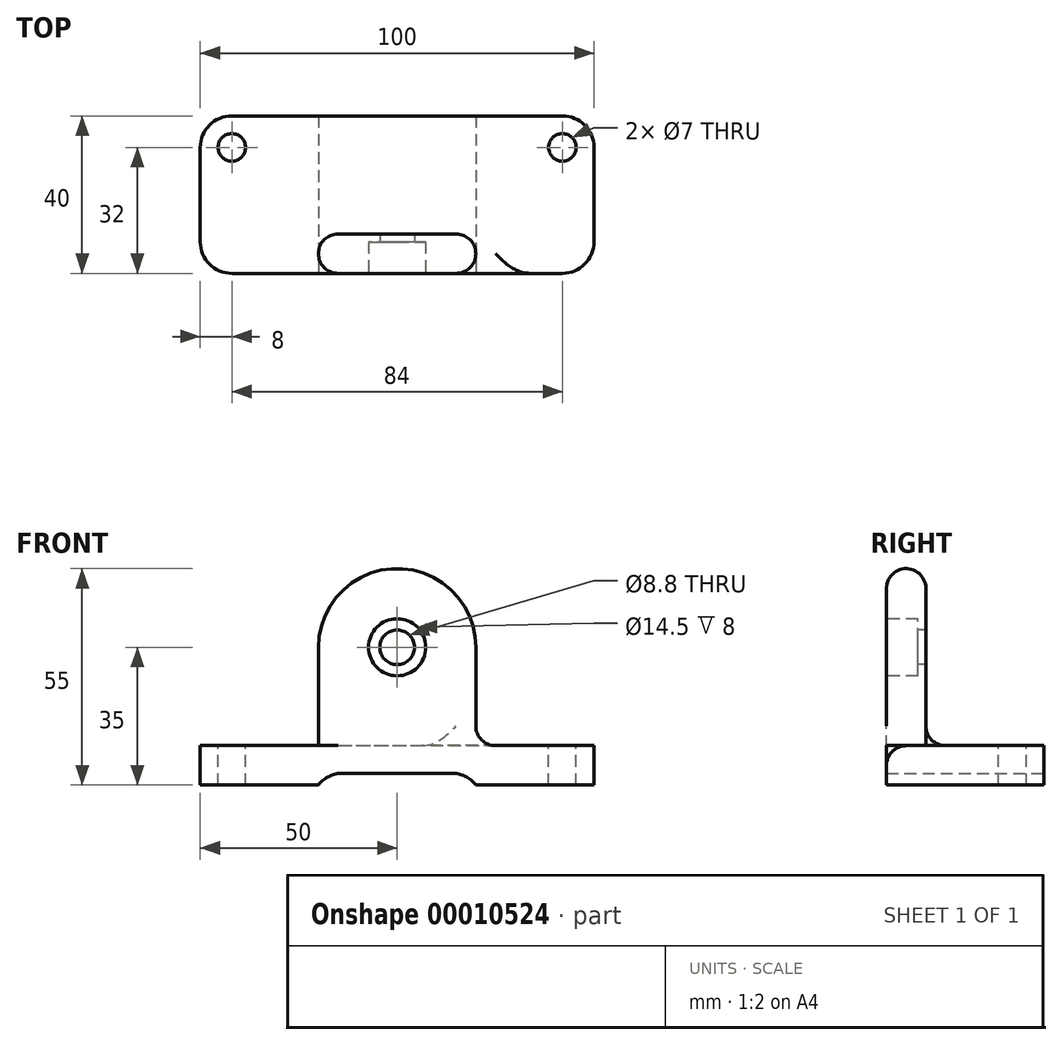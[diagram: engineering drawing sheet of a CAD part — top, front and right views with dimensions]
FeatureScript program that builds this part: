
annotation { "Feature Type Name" : "Feature", "Feature Type Description" : "" }
export const myFeature = defineFeature(function(context is Context, id is Id, definition is map)
    precondition{}
    {
        {
            var Q0;
            Q0=qCreatedBy(makeId("Top.planeOp"),FACE);
            var sketch = newSketch(context, id + "F0", { "sketchPlane" : qUnion([Q0])});
            skLineSegment(sketch, "E0.bottom", {"start": v(0, 0) * mm, "end": v(100, 0) * mm});
            skLineSegment(sketch, "E0.top", {"start": v(0, 40) * mm, "end": v(100, 40) * mm});
            skLineSegment(sketch, "E0.left", {"start": v(0, 0) * mm, "end": v(0, 40) * mm});
            skLineSegment(sketch, "E0.right", {"start": v(100, 0) * mm, "end": v(100, 40) * mm});
            skSolve(sketch);
        }
        {
            var Q0;
            Q0 = qSketchRegion(id + "F0", true);
            extrude(context, id + "F1", {"entities" : qUnion([Q0]), "depth" : 10 * mm});
        }
        {
            var Q0;
            Q0=makeQuery(id+"F1.opExtrude","SWEPT_FACE",FACE,{"disambiguationData":[OSD([sQuery(id+"F0.wireOp",EDGE,"E0.bottom")])]});
            var sketch = newSketch(context, id + "F2", { "sketchPlane" : qUnion([Q0])});
            skLineSegment(sketch, "E1", {"start": v(30, 0) * mm, "end": v(30, 35) * mm});
            skArc(sketch, "E2", {"start": v(30, 35) * mm, "mid": v(50, 55) * mm, "end": v(70, 35) * mm});
            skLineSegment(sketch, "E3", {"start": v(70, 35) * mm, "end": v(70, 0) * mm});
            skLineSegment(sketch, "E4", {"start": v(70, 0) * mm, "end": v(30, 0) * mm});
            skSolve(sketch);
        }
        {
            var Q0;
            Q0 = qSketchRegion(id + "F2", true);
            extrude(context, id + "F3", {"entities" : qUnion([Q0]), "operationType" : NewBodyOperationType.ADD, "oppositeDirection" : true, "depth" : 10 * mm});
        }
        {
            var Q0;
            Q0=makeQuery(id+"F3.boolean.opBoolean","MERGE",FACE,{"derivedFrom":[makeQuery(id+"F1.opExtrude","SWEPT_FACE",FACE,{"disambiguationData":[OSD([sQuery(id+"F0.wireOp",EDGE,"E0.bottom")])]}),makeQuery(id+"F3.opExtrude","CAP_FACE",FACE,{"disambiguationData":[OSD([sQuery(id+"F2.wireOp",EDGE,"E1"),sQuery(id+"F2.wireOp",EDGE,"E2"),sQuery(id+"F2.wireOp",EDGE,"E3"),sQuery(id+"F2.wireOp",EDGE,"E4")])],"isStart":true})]});
            var sketch = newSketch(context, id + "F4", { "sketchPlane" : qUnion([Q0])});
            skLineSegment(sketch, "E5.bottom", {"start": v(30, 0) * mm, "end": v(70, 0) * mm});
            skLineSegment(sketch, "E5.top", {"start": v(30, 3) * mm, "end": v(70, 3) * mm});
            skLineSegment(sketch, "E5.left", {"start": v(30, 0) * mm, "end": v(30, 3) * mm});
            skLineSegment(sketch, "E5.right", {"start": v(70, 0) * mm, "end": v(70, 3) * mm});
            skSolve(sketch);
        }
        {
            var Q0;
            Q0 = qSketchRegion(id + "F4", true);
            extrude(context, id + "F5", {"entities" : qUnion([Q0]), "operationType" : NewBodyOperationType.REMOVE, "endBound" : BoundingType.THROUGH_ALL, "oppositeDirection" : true, "depth" : 25 * mm});
        }
        {
            var Q0;
            Q0=makeQuery(id+"F3.boolean.opBoolean","MERGE",FACE,{"derivedFrom":[makeQuery(id+"F1.opExtrude","SWEPT_FACE",FACE,{"disambiguationData":[OSD([sQuery(id+"F0.wireOp",EDGE,"E0.bottom")])]}),makeQuery(id+"F3.opExtrude","CAP_FACE",FACE,{"disambiguationData":[OSD([sQuery(id+"F2.wireOp",EDGE,"E1"),sQuery(id+"F2.wireOp",EDGE,"E2"),sQuery(id+"F2.wireOp",EDGE,"E3"),sQuery(id+"F2.wireOp",EDGE,"E4")])],"isStart":true})]});
            var sketch = newSketch(context, id + "F6", { "sketchPlane" : qUnion([Q0])});
            skCircle(sketch, "E6", {"center": v(50, 35) * mm, "radius": 4.4 * mm});
            skSolve(sketch);
        }
        {
            var Q0;
            Q0 = qSketchRegion(id + "F6", true);
            extrude(context, id + "F7", {"entities" : qUnion([Q0]), "operationType" : NewBodyOperationType.REMOVE, "endBound" : BoundingType.THROUGH_ALL, "oppositeDirection" : true, "depth" : 25 * mm});
        }
        {
            var Q0;
            Q0=makeQuery(id+"F3.boolean.opBoolean","MERGE",FACE,{"derivedFrom":[makeQuery(id+"F1.opExtrude","SWEPT_FACE",FACE,{"disambiguationData":[OSD([sQuery(id+"F0.wireOp",EDGE,"E0.bottom")])]}),makeQuery(id+"F3.opExtrude","CAP_FACE",FACE,{"disambiguationData":[OSD([sQuery(id+"F2.wireOp",EDGE,"E1"),sQuery(id+"F2.wireOp",EDGE,"E2"),sQuery(id+"F2.wireOp",EDGE,"E3"),sQuery(id+"F2.wireOp",EDGE,"E4")])],"isStart":true})]});
            var sketch = newSketch(context, id + "F8", { "sketchPlane" : qUnion([Q0])});
            skCircle(sketch, "E7", {"center": v(50, 35) * mm, "radius": 7.25 * mm});
            skSolve(sketch);
        }
        {
            var Q0;
            Q0 = qSketchRegion(id + "F8", true);
            extrude(context, id + "F9", {"entities" : qUnion([Q0]), "operationType" : NewBodyOperationType.REMOVE, "oppositeDirection" : true, "depth" : 8 * mm});
        }
        {
            var Q0;
            Q0=makeQuery(id+"F5.boolean.opBoolean","COPY",EDGE,{"derivedFrom":makeQuery(id+"F5.opExtrude","SWEPT_EDGE",EDGE,{"disambiguationData":[OSD([sQuery(id+"F4.wireOp",EDGE,"E5.top"),sQuery(id+"F4.wireOp",EDGE,"E5.left")])]})});
            var Q1;
            Q1=makeQuery(id+"F5.boolean.opBoolean","COPY",EDGE,{"derivedFrom":makeQuery(id+"F5.opExtrude","SWEPT_EDGE",EDGE,{"disambiguationData":[OSD([sQuery(id+"F4.wireOp",EDGE,"E5.top"),sQuery(id+"F4.wireOp",EDGE,"E5.right")])]})});
            var Q2;
            Q2=makeQuery(id+"F1.opExtrude","SWEPT_EDGE",EDGE,{"disambiguationData":[OSD([sQuery(id+"F0.wireOp",EDGE,"E0.bottom"),sQuery(id+"F0.wireOp",EDGE,"E0.right")])]});
            var Q3;
            Q3=makeQuery(id+"F1.opExtrude","SWEPT_EDGE",EDGE,{"disambiguationData":[OSD([sQuery(id+"F0.wireOp",EDGE,"E0.bottom"),sQuery(id+"F0.wireOp",EDGE,"E0.left")])]});
            var Q4;
            Q4=makeQuery(id+"F1.opExtrude","SWEPT_EDGE",EDGE,{"disambiguationData":[OSD([sQuery(id+"F0.wireOp",EDGE,"E0.top"),sQuery(id+"F0.wireOp",EDGE,"E0.left")])]});
            var Q5;
            Q5=makeQuery(id+"F1.opExtrude","SWEPT_EDGE",EDGE,{"disambiguationData":[OSD([sQuery(id+"F0.wireOp",EDGE,"E0.top"),sQuery(id+"F0.wireOp",EDGE,"E0.right")])]});
            fillet(context, id + "F10", {"entities" : qUnion([Q0, Q1, Q2, Q3, Q4, Q5]), "radius" : 8 * mm, "tangentPropagation" : true, "allowEdgeOverflow" : false});
        }
        {
            var Q0;
            Q0=makeQuery(id+"F1.opExtrude","CAP_FACE",FACE,{"disambiguationData":[OSD([sQuery(id+"F0.wireOp",EDGE,"E0.bottom"),sQuery(id+"F0.wireOp",EDGE,"E0.top"),sQuery(id+"F0.wireOp",EDGE,"E0.left"),sQuery(id+"F0.wireOp",EDGE,"E0.right")])],"isStart":false});
            var sketch = newSketch(context, id + "F11", { "sketchPlane" : qUnion([Q0])});
            skCircle(sketch, "E8", {"center": v(8, 32) * mm, "radius": 3.5 * mm});
            skCircle(sketch, "E9", {"center": v(92, 32) * mm, "radius": 3.5 * mm});
            skSolve(sketch);
        }
        {
            var Q0;
            Q0 = qSketchRegion(id + "F11", true);
            extrude(context, id + "F12", {"entities" : qUnion([Q0]), "operationType" : NewBodyOperationType.REMOVE, "endBound" : BoundingType.THROUGH_ALL, "oppositeDirection" : true, "depth" : 25 * mm});
        }
        {
            var Q0;
            Q0=makeQuery(id+"F3.opExtrude","CAP_EDGE",EDGE,{"disambiguationData":[OSD([sQuery(id+"F2.wireOp",EDGE,"E2")])],"isStart":false});
            var Q1;
            Q1=makeQuery(id+"F3.opExtrude","CAP_EDGE",EDGE,{"disambiguationData":[OSD([sQuery(id+"F2.wireOp",EDGE,"E2")])],"isStart":true});
            var Q2;
            Q2=makeQuery(id+"F3.opExtrude","CAP_EDGE",EDGE,{"disambiguationData":[OSD([sQuery(id+"F2.wireOp",EDGE,"E3")])],"isStart":true});
            var Q3;
            Q3=makeQuery(id+"F3.boolean.opBoolean","INTERSECT",EDGE,{"derivedFrom":[makeQuery(id+"F1.opExtrude","CAP_FACE",FACE,{"disambiguationData":[OSD([sQuery(id+"F0.wireOp",EDGE,"E0.bottom"),sQuery(id+"F0.wireOp",EDGE,"E0.top"),sQuery(id+"F0.wireOp",EDGE,"E0.left"),sQuery(id+"F0.wireOp",EDGE,"E0.right")])],"isStart":false}),makeQuery(id+"F3.opExtrude","SWEPT_FACE",FACE,{"disambiguationData":[OSD([sQuery(id+"F2.wireOp",EDGE,"E3")])]})]});
            fillet(context, id + "F13", {"entities" : qUnion([Q0, Q1, Q2, Q3]), "radius" : 5 * mm, "tangentPropagation" : true, "allowEdgeOverflow" : false});
        }
    });
